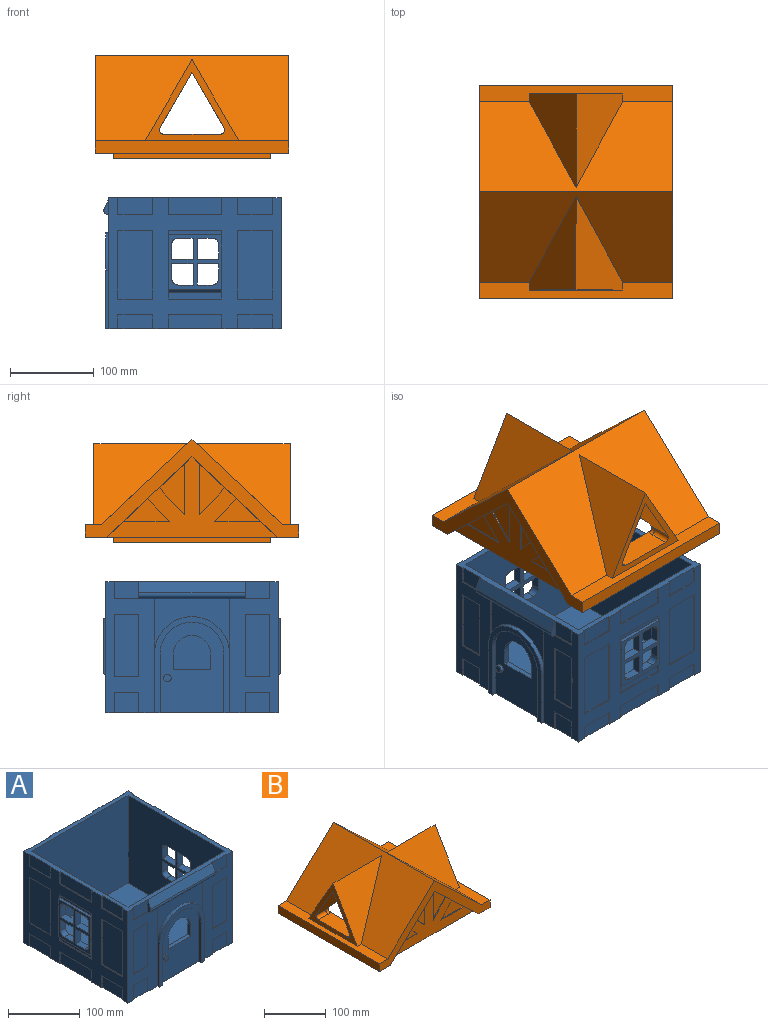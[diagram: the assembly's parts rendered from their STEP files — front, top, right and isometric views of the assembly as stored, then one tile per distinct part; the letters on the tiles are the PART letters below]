
ASSEMBLY  parts=2 mates=1
PART A: 231 faces, bbox 210.8x211.7x156.2 mm
  f0: plane 66.04x20.32mm, normal (0,1,0), area 1341.9mm2, adj f7,f219,f220,f223
  f1: plane 41.66x20.32mm, normal (0,1,0), area 846.4mm2, adj f7,f216,f217,f218
  f2: plane 66.04x20.32mm, normal (0,1,0), area 1341.9mm2, adj f6,f210,f211,f212
  f3: plane 41.66x20.32mm, normal (0,1,0), area 846.4mm2, adj f6,f207,f208,f209
  f4: plane 41.66x20.32mm, normal (0,1,0), area 846.4mm2, adj f6,f213,f214,f215
  f5: plane 41.66x20.32mm, normal (0,1,0), area 846.4mm2, adj f7,f204,f205,f206
  f6: plane 209.55x205.74mm, normal (0,0,-1), area 41647mm2, adj f2,f3,f4,f14,f15,f16,f19,f21
  f7: plane 205.74x205.74mm, normal (0,0,1), area 5328.9mm2, adj f0,f1,f5,f8,f15,f22,f23,f24
  f8: plane 20.32x1.27mm, normal (-1,0,0), area 25.8mm2, adj f7,f9,f15,f41
  f9: plane 28.7x1.27mm, normal (0,0,1), area 36.5mm2, adj f8,f15,f41,f104
  f10: plane 28.7x1.27mm, normal (0,0,-1), area 36.5mm2, adj f11,f15,f17,f18
  f11: plane 74.17x1.27mm, normal (-1,0,0), area 94.2mm2, adj f10,f12,f15,f17
  f12: plane 28.7x1.27mm, normal (0,0,1), area 36.5mm2, adj f11,f15,f17,f18
  f13: plane 28.7x1.27mm, normal (0,0,-1), area 36.5mm2, adj f14,f15,f16,f19
  f14: plane 24.13x1.27mm, normal (-1,0,0), area 30.6mm2, adj f6,f13,f15,f16
  f15: plane 156.21x58.17mm, normal (0,-1,0), area 5299.6mm2, adj f6,f7,f8,f9,f10,f11,f12,f13
  f16: plane 28.7x24.13mm, normal (0,-1,0), area 692.6mm2, adj f6,f13,f14,f19
  f17: plane 74.17x28.7mm, normal (0,-1,0), area 2128.8mm2, adj f10,f11,f12,f18
  f18: plane 74.17x1.27mm, normal (1,0,0), area 94.2mm2, adj f10,f12,f15,f17
  f19: plane 24.13x1.27mm, normal (1,0,0), area 30.6mm2, adj f6,f13,f15,f16
  f20: plane 74.17x28.7mm, normal (0,-1,0), area 2128.8mm2, adj f30,f151,f152,f153
  f21: plane 28.7x24.13mm, normal (0,-1,0), area 692.6mm2, adj f6,f103,f149,f150
  f22: plane 41.66x20.32mm, normal (-1,0,0), area 846.4mm2, adj f7,f176,f177,f178
  f23: plane 63.5x20.32mm, normal (-1,0,0), area 1290.3mm2, adj f7,f173,f174,f175
  f24: plane 41.66x20.32mm, normal (-1,0,0), area 846.4mm2, adj f7,f170,f171,f172
  f25: plane 41.66x20.32mm, normal (-1,0,0), area 846.4mm2, adj f6,f167,f168,f169
  f26: plane 63.5x4.06mm, normal (-1,0,0), area 258.1mm2, adj f145,f146,f182,f230
  f27: plane 63.5x5.33mm, normal (-1,0,0), area 338.7mm2, adj f81,f158,f159,f160
  f28: plane 63.5x20.32mm, normal (-1,0,0), area 1290.3mm2, adj f6,f164,f165,f166
  f29: plane 41.66x20.32mm, normal (-1,0,0), area 846.4mm2, adj f6,f179,f180,f181
  f30: plane 74.17x1.27mm, normal (-1,0,0), area 94.2mm2, adj f20,f108,f151,f153
  f31: plane 20.32x7.27mm, normal (-1,0,0), area 95.6mm2, adj f7,f43,f44,f105,f109,f147
  f32: plane 63.5x20.32mm, normal (1,0,0), area 1290.3mm2, adj f7,f121,f137,f140
  f33: plane 41.66x20.32mm, normal (1,0,0), area 846.4mm2, adj f7,f134,f135,f136
  f34: plane 63.5x16.51mm, normal (1,0,0), area 1048.4mm2, adj f6,f128,f129,f130
  f35: plane 41.66x16.51mm, normal (1,0,0), area 687.7mm2, adj f6,f125,f126,f127
  f36: plane 41.66x20.32mm, normal (1,0,0), area 846.4mm2, adj f7,f122,f123,f124
  f37: plane 41.66x16.51mm, normal (1,0,0), area 687.7mm2, adj f6,f131,f132,f133
  f38: plane 63.5x7.87mm, normal (1,0,0), area 500mm2, adj f110,f111,f141,f229
  f39: plane 63.5x5.33mm, normal (1,0,0), area 338.7mm2, adj f61,f112,f113,f114
  f40: plane 89.41x66.04mm, normal (0,-1,0), area 2765.4mm2, adj f43,f52,f106,f107
  f41: plane 28.7x20.32mm, normal (0,-1,0), area 583.2mm2, adj f7,f8,f9,f104
  f42: plane 69.85x3.81mm, normal (1,0,0), area 266.1mm2, adj f6,f15,f52,f56
  f43: plane 127x2.19mm, normal (0,0,-1), area 229.9mm2, adj f15,f31,f40,f104,f106,f107,f108,f109
  f44: plane 28.7x20.32mm, normal (0,-1,0), area 583.2mm2, adj f7,f31,f147,f148
  f45: plane 190.5x149.86mm, normal (1,0,0), area 26017.5mm2, adj f7,f48,f49,f50,f83,f84,f85,f86
  f46: plane 190.5x149.86mm, normal (-1,0,0), area 26017.5mm2, adj f7,f48,f49,f50,f63,f64,f65,f66
  f47: plane 107.95x76.2mm, normal (0,-1,0), area 5923.2mm2, adj f6,f51,f54,f55,f57,f58,f59,f60
  f48: plane 190.5x149.86mm, normal (0,1,0), area 26935.1mm2, adj f7,f45,f46,f50,f57,f58,f59,f60
  f49: plane 190.5x149.86mm, normal (0,-1,0), area 28548.3mm2, adj f7,f45,f46,f50
  f50: plane 190.5x190.5mm, normal (0,0,1), area 36290.2mm2, adj f45,f46,f48,f49
  f51: plane 69.85x5.08mm, normal (-1,0,0), area 354.8mm2, adj f6,f47,f55,f56
  f52: cylinder r=44.7mm len=89.41mm, axis (0,1,0), area 713.4mm2, adj f40,f42,f53,f56,f106,f107
  f53: plane 69.85x3.81mm, normal (-1,0,0), area 266.1mm2, adj f6,f52,f56,f108
  f54: plane 69.85x5.08mm, normal (1,0,0), area 354.8mm2, adj f6,f47,f55,f56
  f55: cylinder r=38.1mm len=76.2mm, axis (0,1,0), area 608mm2, adj f47,f51,f54,f56
  f56: plane 114.55x89.41mm, normal (0,-1,0), area 1781.6mm2, adj f6,f42,f51,f52,f53,f54,f55
  f57: plane 18.84x6.35mm, normal (1,0,0), area 119.6mm2, adj f47,f48,f58,f59
  f58: cylinder r=22.23mm len=44.45mm, axis (0,-1,0), area 443.4mm2, adj f47,f48,f57,f60
  f59: plane 44.45x6.35mm, normal (0,0,1), area 282.3mm2, adj f47,f48,f57,f60
  f60: plane 18.84x6.35mm, normal (-1,0,0), area 119.6mm2, adj f47,f48,f58,f59
  f61: plane 63.5x3.81mm, normal (0,0,1), area 241.9mm2, adj f39,f62,f79,f80,f112,f114
  f62: plane 67.31x2.54mm, normal (0,-1,0), area 167.7mm2, adj f61,f80,f142,f229
  f63: plane 17.78x10.16mm, normal (0,1,0), area 180.6mm2, adj f46,f75,f80,f194
  f64: plane 17.78x10.16mm, normal (0,0,-1), area 180.6mm2, adj f46,f65,f80,f194
  f65: plane 25.4x10.16mm, normal (0,-1,0), area 258.1mm2, adj f46,f64,f75,f80
  f66: plane 17.78x10.16mm, normal (0,0,1), area 180.6mm2, adj f46,f76,f80,f193
  f67: plane 17.78x10.16mm, normal (0,1,0), area 180.6mm2, adj f46,f68,f80,f193
  f68: plane 25.4x10.16mm, normal (0,0,-1), area 258.1mm2, adj f46,f67,f76,f80
  f69: plane 25.4x10.16mm, normal (0,0,1), area 258.1mm2, adj f46,f70,f77,f80
  f70: plane 25.4x10.16mm, normal (0,1,0), area 258.1mm2, adj f46,f69,f71,f80
  f71: plane 17.78x10.16mm, normal (0,0,-1), area 180.6mm2, adj f46,f70,f80,f192
  f72: plane 17.78x10.16mm, normal (0,0,1), area 180.6mm2, adj f46,f73,f80,f191
  f73: plane 25.4x10.16mm, normal (0,1,0), area 258.1mm2, adj f46,f72,f74,f80
  f74: plane 25.4x10.16mm, normal (0,0,-1), area 258.1mm2, adj f46,f73,f78,f80
  f75: plane 25.4x10.16mm, normal (0,0,1), area 258.1mm2, adj f46,f63,f65,f80
  f76: plane 25.4x10.16mm, normal (0,-1,0), area 258.1mm2, adj f46,f66,f68,f80
  f77: plane 17.78x10.16mm, normal (0,-1,0), area 180.6mm2, adj f46,f69,f80,f192
  f78: plane 17.78x10.16mm, normal (0,-1,0), area 180.6mm2, adj f46,f74,f80,f191
  f79: plane 67.31x2.54mm, normal (0,1,0), area 167.7mm2, adj f61,f80,f142,f229
  f80: plane 64.77x63.5mm, normal (1,0,0), area 1582.1mm2, adj f61,f62,f63,f64,f65,f66,f67,f68
  f81: plane 63.5x3.81mm, normal (0,0,1), area 241.9mm2, adj f27,f82,f99,f100,f158,f160
  f82: plane 67.31x2.54mm, normal (0,1,0), area 167.7mm2, adj f81,f100,f154,f230
  f83: plane 17.78x10.16mm, normal (0,-1,0), area 180.6mm2, adj f45,f95,f100,f190
  f84: plane 17.78x10.16mm, normal (0,0,-1), area 180.6mm2, adj f45,f85,f100,f190
  f85: plane 25.4x10.16mm, normal (0,1,0), area 258.1mm2, adj f45,f84,f95,f100
  f86: plane 17.78x10.16mm, normal (0,0,1), area 180.6mm2, adj f45,f96,f100,f189
  f87: plane 17.78x10.16mm, normal (0,-1,0), area 180.6mm2, adj f45,f88,f100,f189
  f88: plane 25.4x10.16mm, normal (0,0,-1), area 258.1mm2, adj f45,f87,f96,f100
  f89: plane 25.4x10.16mm, normal (0,0,1), area 258.1mm2, adj f45,f90,f97,f100
  f90: plane 25.4x10.16mm, normal (0,-1,0), area 258.1mm2, adj f45,f89,f91,f100
  f91: plane 17.78x10.16mm, normal (0,0,-1), area 180.6mm2, adj f45,f90,f100,f188
  f92: plane 17.78x10.16mm, normal (0,0,1), area 180.6mm2, adj f45,f93,f100,f187
  f93: plane 25.4x10.16mm, normal (0,-1,0), area 258.1mm2, adj f45,f92,f94,f100
  f94: plane 25.4x10.16mm, normal (0,0,-1), area 258.1mm2, adj f45,f93,f98,f100
  f95: plane 25.4x10.16mm, normal (0,0,1), area 258.1mm2, adj f45,f83,f85,f100
  f96: plane 25.4x10.16mm, normal (0,1,0), area 258.1mm2, adj f45,f86,f88,f100
  f97: plane 17.78x10.16mm, normal (0,1,0), area 180.6mm2, adj f45,f89,f100,f188
  f98: plane 17.78x10.16mm, normal (0,1,0), area 180.6mm2, adj f45,f94,f100,f187
  f99: plane 67.31x2.54mm, normal (0,-1,0), area 167.7mm2, adj f81,f100,f154,f230
  f100: plane 64.77x63.5mm, normal (-1,0,0), area 1582.1mm2, adj f81,f82,f83,f84,f85,f86,f87,f88
  f101: cylinder r=4.59mm len=9.19mm, axis (0,1,0), area 110mm2, adj f47,f102
  f102: plane 9.19x9.19mm, normal (0,-1,0), area 66.3mm2, adj f101
  f103: plane 24.13x1.27mm, normal (-1,0,0), area 30.6mm2, adj f6,f21,f108,f150
  f104: plane 20.32x7.27mm, normal (1,0,0), area 95.6mm2, adj f7,f9,f41,f43,f105,f109
  f105: plane 127x13.09mm, normal (0,-0.91,0.42), area 1834.7mm2, adj f7,f31,f104,f109
  f106: plane 66.04x1.27mm, normal (-1,0,0), area 83.9mm2, adj f15,f40,f43,f52
  f107: plane 66.04x1.27mm, normal (1,0,0), area 83.9mm2, adj f40,f43,f52,f108
  f108: plane 156.21x58.17mm, normal (0,-1,0), area 5299.6mm2, adj f6,f7,f30,f43,f53,f103,f107,f147
  f109: cylinder r=5.08mm len=127mm, axis (-1,0,0), area 1294.9mm2, adj f31,f43,f104,f105
  f110: plane 9.14x1.27mm, normal (0,1,0), area 10.8mm2, adj f38,f141,f142,f229
  f111: plane 9.14x1.27mm, normal (0,-1,0), area 10.8mm2, adj f38,f141,f142,f229
  f112: plane 5.33x1.27mm, normal (0,1,0), area 6.8mm2, adj f39,f61,f113,f142
  f113: plane 63.5x1.27mm, normal (0,0,-1), area 80.6mm2, adj f39,f112,f114,f142
  f114: plane 5.33x1.27mm, normal (0,-1,0), area 6.8mm2, adj f39,f61,f113,f142
  f115: plane 81.79x1.27mm, normal (0,-1,0), area 103.9mm2, adj f116,f138,f142,f144
  f116: plane 41.66x1.27mm, normal (0,0,1), area 52.9mm2, adj f115,f117,f142,f144
  f117: plane 81.79x1.27mm, normal (0,1,0), area 103.9mm2, adj f116,f138,f142,f144
  f118: plane 41.66x1.27mm, normal (0,0,1), area 52.9mm2, adj f119,f139,f142,f143
  f119: plane 81.79x1.27mm, normal (0,1,0), area 103.9mm2, adj f118,f120,f142,f143
  f120: plane 41.66x1.27mm, normal (0,0,-1), area 52.9mm2, adj f119,f139,f142,f143
  f121: plane 20.32x1.27mm, normal (0,1,0), area 25.8mm2, adj f7,f32,f140,f142
  f122: plane 20.32x1.27mm, normal (0,-1,0), area 25.8mm2, adj f7,f36,f123,f142
  f123: plane 41.66x1.27mm, normal (0,0,1), area 52.9mm2, adj f36,f122,f124,f142
  f124: plane 20.32x1.27mm, normal (0,1,0), area 25.8mm2, adj f7,f36,f123,f142
  f125: plane 16.51x1.27mm, normal (0,1,0), area 21mm2, adj f6,f35,f126,f142
  f126: plane 41.66x1.27mm, normal (0,0,-1), area 52.9mm2, adj f35,f125,f127,f142
  f127: plane 16.51x1.27mm, normal (0,-1,0), area 21mm2, adj f6,f35,f126,f142
  f128: plane 16.51x1.27mm, normal (0,1,0), area 21mm2, adj f6,f34,f129,f142
  f129: plane 63.5x1.27mm, normal (0,0,-1), area 80.6mm2, adj f34,f128,f130,f142
  f130: plane 16.51x1.27mm, normal (0,-1,0), area 21mm2, adj f6,f34,f129,f142
  f131: plane 16.51x1.27mm, normal (0,1,0), area 21mm2, adj f6,f37,f132,f142
  f132: plane 41.66x1.27mm, normal (0,0,-1), area 52.9mm2, adj f37,f131,f133,f142
  f133: plane 16.51x1.27mm, normal (0,-1,0), area 21mm2, adj f6,f37,f132,f142
  f134: plane 20.32x1.27mm, normal (0,-1,0), area 25.8mm2, adj f7,f33,f135,f142
  f135: plane 41.66x1.27mm, normal (0,0,1), area 52.9mm2, adj f33,f134,f136,f142
  f136: plane 20.32x1.27mm, normal (0,1,0), area 25.8mm2, adj f7,f33,f135,f142
  f137: plane 20.32x1.27mm, normal (0,-1,0), area 25.8mm2, adj f7,f32,f140,f142
  f138: plane 41.66x1.27mm, normal (0,0,-1), area 52.9mm2, adj f115,f117,f142,f144
  f139: plane 81.79x1.27mm, normal (0,-1,0), area 103.9mm2, adj f118,f120,f142,f143
  f140: plane 63.5x1.27mm, normal (0,0,1), area 80.6mm2, adj f32,f121,f137,f142
  f141: plane 63.5x1.27mm, normal (0,0,1), area 80.6mm2, adj f38,f110,f111,f142
  f142: plane 205.74x156.21mm, normal (1,0,0), area 14724.1mm2, adj f6,f7,f15,f62,f79,f110,f111,f112
  f143: plane 81.79x41.66mm, normal (1,0,0), area 3407mm2, adj f118,f119,f120,f139
  f144: plane 81.79x41.66mm, normal (1,0,0), area 3407mm2, adj f115,f116,f117,f138
  f145: plane 5.33x1.27mm, normal (0,-1,0), area 6mm2, adj f26,f154,f182,f230
  f146: plane 5.33x1.27mm, normal (0,1,0), area 6mm2, adj f26,f154,f182,f230
  f147: plane 28.7x1.27mm, normal (0,0,1), area 36.5mm2, adj f31,f44,f108,f148
  f148: plane 20.32x1.27mm, normal (1,0,0), area 25.8mm2, adj f7,f44,f108,f147
  f149: plane 24.13x1.27mm, normal (1,0,0), area 30.6mm2, adj f6,f21,f108,f150
  f150: plane 28.7x1.27mm, normal (0,0,-1), area 36.5mm2, adj f21,f103,f108,f149
  f151: plane 28.7x1.27mm, normal (0,0,1), area 36.5mm2, adj f20,f30,f108,f152
  f152: plane 74.17x1.27mm, normal (1,0,0), area 94.2mm2, adj f20,f108,f151,f153
  f153: plane 28.7x1.27mm, normal (0,0,-1), area 36.5mm2, adj f20,f30,f108,f152
  f154: plane 205.74x156.21mm, normal (-1,0,0), area 14724.1mm2, adj f6,f7,f82,f99,f108,f145,f146,f155
  f155: plane 77.98x1.27mm, normal (0,-1,0), area 99mm2, adj f154,f156,f184,f185
  f156: plane 41.66x1.27mm, normal (0,0,-1), area 52.9mm2, adj f154,f155,f157,f185
  f157: plane 77.98x1.27mm, normal (0,1,0), area 99mm2, adj f154,f156,f184,f185
  f158: plane 5.33x1.27mm, normal (0,-1,0), area 6.8mm2, adj f27,f81,f154,f159
  f159: plane 63.5x1.27mm, normal (0,0,-1), area 80.6mm2, adj f27,f154,f158,f160
  f160: plane 5.33x1.27mm, normal (0,1,0), area 6.8mm2, adj f27,f81,f154,f159
  f161: plane 77.98x1.27mm, normal (0,-1,0), area 99mm2, adj f154,f162,f183,f186
  f162: plane 41.66x1.27mm, normal (0,0,-1), area 52.9mm2, adj f154,f161,f163,f186
  f163: plane 77.98x1.27mm, normal (0,1,0), area 99mm2, adj f154,f162,f183,f186
  f164: plane 20.32x1.27mm, normal (0,-1,0), area 25.8mm2, adj f6,f28,f154,f165
  f165: plane 63.5x1.27mm, normal (0,0,-1), area 80.6mm2, adj f28,f154,f164,f166
  f166: plane 20.32x1.27mm, normal (0,1,0), area 25.8mm2, adj f6,f28,f154,f165
  f167: plane 20.32x1.27mm, normal (0,-1,0), area 25.8mm2, adj f6,f25,f154,f168
  f168: plane 41.66x1.27mm, normal (0,0,-1), area 52.9mm2, adj f25,f154,f167,f169
  f169: plane 20.32x1.27mm, normal (0,1,0), area 25.8mm2, adj f6,f25,f154,f168
  f170: plane 20.32x1.27mm, normal (0,1,0), area 25.8mm2, adj f7,f24,f154,f171
  f171: plane 41.66x1.27mm, normal (0,0,1), area 52.9mm2, adj f24,f154,f170,f172
  f172: plane 20.32x1.27mm, normal (0,-1,0), area 25.8mm2, adj f7,f24,f154,f171
  f173: plane 20.32x1.27mm, normal (0,1,0), area 25.8mm2, adj f7,f23,f154,f174
  f174: plane 63.5x1.27mm, normal (0,0,1), area 80.6mm2, adj f23,f154,f173,f175
  f175: plane 20.32x1.27mm, normal (0,-1,0), area 25.8mm2, adj f7,f23,f154,f174
  f176: plane 20.32x1.27mm, normal (0,1,0), area 25.8mm2, adj f7,f22,f154,f177
  f177: plane 41.66x1.27mm, normal (0,0,1), area 52.9mm2, adj f22,f154,f176,f178
  f178: plane 20.32x1.27mm, normal (0,-1,0), area 25.8mm2, adj f7,f22,f154,f177
  f179: plane 20.32x1.27mm, normal (0,-1,0), area 25.8mm2, adj f6,f29,f154,f180
  f180: plane 41.66x1.27mm, normal (0,0,-1), area 52.9mm2, adj f29,f154,f179,f181
  f181: plane 20.32x1.27mm, normal (0,1,0), area 25.8mm2, adj f6,f29,f154,f180
  f182: plane 63.5x1.27mm, normal (0,0,1), area 80.6mm2, adj f26,f145,f146,f154
  f183: plane 41.66x1.27mm, normal (0,0,1), area 52.9mm2, adj f154,f161,f163,f186
  f184: plane 41.66x1.27mm, normal (0,0,1), area 52.9mm2, adj f154,f155,f157,f185
  f185: plane 77.98x41.66mm, normal (-1,0,0), area 3248.3mm2, adj f155,f156,f157,f184
  f186: plane 77.98x41.66mm, normal (-1,0,0), area 3248.3mm2, adj f161,f162,f163,f183
  f187: cylinder r=7.62mm len=10.16mm, axis (1,0,0), area 121.6mm2, adj f45,f92,f98,f100
  f188: cylinder r=7.62mm len=10.16mm, axis (-1,0,0), area 121.6mm2, adj f45,f91,f97,f100
  f189: cylinder r=7.62mm len=10.16mm, axis (-1,0,0), area 121.6mm2, adj f45,f86,f87,f100
  f190: cylinder r=7.62mm len=10.16mm, axis (1,0,0), area 121.6mm2, adj f45,f83,f84,f100
  f191: cylinder r=7.62mm len=10.16mm, axis (-1,0,0), area 121.6mm2, adj f46,f72,f78,f80
  f192: cylinder r=7.62mm len=10.16mm, axis (1,0,0), area 121.6mm2, adj f46,f71,f77,f80
  f193: cylinder r=7.62mm len=10.16mm, axis (1,0,0), area 121.6mm2, adj f46,f66,f67,f80
  f194: cylinder r=7.62mm len=10.16mm, axis (-1,0,0), area 121.6mm2, adj f46,f63,f64,f80
  f195: plane 41.66x1.27mm, normal (0,0,-1), area 52.9mm2, adj f196,f224,f225,f228
  f196: plane 77.98x1.27mm, normal (1,0,0), area 99mm2, adj f195,f197,f225,f228
  f197: plane 41.66x1.27mm, normal (0,0,1), area 52.9mm2, adj f196,f224,f225,f228
  f198: plane 77.98x1.27mm, normal (-1,0,0), area 99mm2, adj f199,f221,f225,f227
  f199: plane 66.04x1.27mm, normal (0,0,-1), area 83.9mm2, adj f198,f200,f225,f227
  f200: plane 77.98x1.27mm, normal (1,0,0), area 99mm2, adj f199,f221,f225,f227
  f201: plane 77.98x1.27mm, normal (-1,0,0), area 99mm2, adj f202,f222,f225,f226
  f202: plane 41.66x1.27mm, normal (0,0,-1), area 52.9mm2, adj f201,f203,f225,f226
  f203: plane 77.98x1.27mm, normal (1,0,0), area 99mm2, adj f202,f222,f225,f226
  f204: plane 20.32x1.27mm, normal (1,0,0), area 25.8mm2, adj f5,f7,f205,f225
  f205: plane 41.66x1.27mm, normal (0,0,1), area 52.9mm2, adj f5,f204,f206,f225
  f206: plane 20.32x1.27mm, normal (-1,0,0), area 25.8mm2, adj f5,f7,f205,f225
  f207: plane 20.32x1.27mm, normal (-1,0,0), area 25.8mm2, adj f3,f6,f208,f225
  f208: plane 41.66x1.27mm, normal (0,0,-1), area 52.9mm2, adj f3,f207,f209,f225
  f209: plane 20.32x1.27mm, normal (1,0,0), area 25.8mm2, adj f3,f6,f208,f225
  f210: plane 20.32x1.27mm, normal (-1,0,0), area 25.8mm2, adj f2,f6,f211,f225
  f211: plane 66.04x1.27mm, normal (0,0,-1), area 83.9mm2, adj f2,f210,f212,f225
  f212: plane 20.32x1.27mm, normal (1,0,0), area 25.8mm2, adj f2,f6,f211,f225
  f213: plane 20.32x1.27mm, normal (-1,0,0), area 25.8mm2, adj f4,f6,f214,f225
  f214: plane 41.66x1.27mm, normal (0,0,-1), area 52.9mm2, adj f4,f213,f215,f225
  f215: plane 20.32x1.27mm, normal (1,0,0), area 25.8mm2, adj f4,f6,f214,f225
  f216: plane 20.32x1.27mm, normal (1,0,0), area 25.8mm2, adj f1,f7,f217,f225
  f217: plane 41.66x1.27mm, normal (0,0,1), area 52.9mm2, adj f1,f216,f218,f225
  f218: plane 20.32x1.27mm, normal (-1,0,0), area 25.8mm2, adj f1,f7,f217,f225
  f219: plane 20.32x1.27mm, normal (1,0,0), area 25.8mm2, adj f0,f7,f220,f225
  f220: plane 66.04x1.27mm, normal (0,0,1), area 83.9mm2, adj f0,f219,f223,f225
  f221: plane 66.04x1.27mm, normal (0,0,1), area 83.9mm2, adj f198,f200,f225,f227
  f222: plane 41.66x1.27mm, normal (0,0,1), area 52.9mm2, adj f201,f203,f225,f226
  f223: plane 20.32x1.27mm, normal (-1,0,0), area 25.8mm2, adj f0,f7,f220,f225
  f224: plane 77.98x1.27mm, normal (-1,0,0), area 99mm2, adj f195,f197,f225,f228
  f225: plane 205.74x156.21mm, normal (0,1,0), area 14422.8mm2, adj f6,f7,f142,f154,f195,f196,f197,f198
  f226: plane 77.98x41.66mm, normal (0,1,0), area 3248.3mm2, adj f201,f202,f203,f222
  f227: plane 77.98x66.04mm, normal (0,1,0), area 5149.7mm2, adj f198,f199,f200,f221
  f228: plane 77.98x41.66mm, normal (0,1,0), area 3248.3mm2, adj f195,f196,f197,f224
  f229: plane 63.5x3.81mm, normal (0.71,0,-0.71), area 342.1mm2, adj f38,f62,f79,f80,f110,f111
  f230: plane 63.5x3.81mm, normal (-0.71,0,-0.71), area 342.1mm2, adj f26,f82,f99,f100,f145,f146
PART B: 92 faces, bbox 254x231.1x123.2 mm
  f0: bspline ~16.69x7.15mm, area 36.6mm2, adj f67,f74,f91
  f1: bspline ~16.69x7.15mm, area 37.1mm2, adj f67,f79,f87
  f2: bspline ~16.69x7.15mm, area 37.1mm2, adj f73,f76,f84
  f3: bspline ~16.69x7.15mm, area 36.6mm2, adj f73,f77,f82
  f4: plane 69.41x29.52mm, normal (0,0,1), area 1995.8mm2, adj f49,f67,f86,f88,f89,f90
  f5: plane 231.14x107.66mm, normal (0.69,0,0.73), area 26378.6mm2, adj f6,f11,f15,f16,f53,f54
  f6: plane 231.14x107.66mm, normal (-0.69,0,0.73), area 26378.6mm2, adj f5,f7,f11,f16,f50,f51
  f7: plane 231.14x19.34mm, normal (0,0,1), area 3447.7mm2, adj f6,f11,f16,f17,f49,f50,f51
  f8: plane 254x231.14mm, normal (0,0,-1), area 18392mm2, adj f9,f10,f11,f12,f13,f14,f16,f17
  f9: plane 101.6x95.88mm, normal (0.69,0,-0.73), area 1876.5mm2, adj f8,f10,f16,f21,f22,f30,f31,f32
  f10: plane 101.6x95.88mm, normal (-0.69,0,-0.73), area 1876.5mm2, adj f8,f9,f16,f23,f24,f26,f27,f28
  f11: plane 254x116.84mm, normal (0,1,0), area 5066.9mm2, adj f5,f6,f7,f8,f12,f13,f14,f15
  f12: plane 101.6x95.88mm, normal (0.69,0,-0.73), area 1876.5mm2, adj f8,f11,f13,f19,f25,f37,f38,f39
  f13: plane 101.6x95.88mm, normal (-0.69,0,-0.73), area 1876.5mm2, adj f8,f11,f12,f18,f20,f35,f36,f41
  f14: plane 231.14x15.24mm, normal (1,0,0), area 3522.6mm2, adj f8,f11,f15,f16
  f15: plane 231.14x19.34mm, normal (0,0,1), area 3447.7mm2, adj f5,f11,f14,f16,f52,f53,f54
  f16: plane 254x116.84mm, normal (0,-1,0), area 5066.9mm2, adj f5,f6,f7,f8,f9,f10,f14,f15
  f17: plane 231.14x15.24mm, normal (-1,0,0), area 3522.6mm2, adj f7,f8,f11,f16
  f18: plane 59.63x29.76mm, normal (0,1,0), area 887.4mm2, adj f13,f41,f42
  f19: plane 59.63x29.76mm, normal (0,1,0), area 887.4mm2, adj f12,f39,f40
  f20: plane 54.55x27.23mm, normal (0,1,0), area 742.6mm2, adj f13,f35,f36
  f21: plane 54.55x27.23mm, normal (0,-1,0), area 742.6mm2, adj f9,f32,f33
  f22: plane 59.63x29.76mm, normal (0,-1,0), area 887.4mm2, adj f9,f30,f31
  f23: plane 59.63x29.76mm, normal (0,-1,0), area 887.4mm2, adj f10,f28,f29
  f24: plane 54.55x27.23mm, normal (0,-1,0), area 742.6mm2, adj f10,f26,f27
  f25: plane 54.55x27.23mm, normal (0,1,0), area 742.6mm2, adj f12,f37,f38
  f26: plane 54.55x1.27mm, normal (0,0,1), area 69.3mm2, adj f10,f24,f27,f34
  f27: plane 27.23x25.7mm, normal (0.73,0,-0.69), area 47.5mm2, adj f10,f24,f26,f34
  f28: plane 31.54x29.76mm, normal (-0.73,0,0.69), area 55.1mm2, adj f10,f23,f29,f34
  f29: plane 59.63x1.27mm, normal (1,0,0), area 75.7mm2, adj f10,f23,f28,f34
  f30: plane 59.63x1.27mm, normal (-1,0,0), area 75.7mm2, adj f9,f22,f31,f34
  f31: plane 31.54x29.76mm, normal (0.73,0,0.69), area 55.1mm2, adj f9,f22,f30,f34
  f32: plane 27.23x25.7mm, normal (-0.73,0,-0.69), area 47.5mm2, adj f9,f21,f33,f34
  f33: plane 54.55x1.27mm, normal (0,0,1), area 69.3mm2, adj f9,f21,f32,f34
  f34: plane 203.2x95.88mm, normal (0,-1,0), area 6481.7mm2, adj f8,f9,f10,f26,f27,f28,f29,f30
  f35: plane 27.23x25.7mm, normal (0.73,0,-0.69), area 47.5mm2, adj f13,f20,f36,f43
  f36: plane 54.55x1.27mm, normal (0,0,1), area 69.3mm2, adj f13,f20,f35,f43
  f37: plane 54.55x1.27mm, normal (0,0,1), area 69.3mm2, adj f12,f25,f38,f43
  f38: plane 27.23x25.7mm, normal (-0.73,0,-0.69), area 47.5mm2, adj f12,f25,f37,f43
  f39: plane 31.54x29.76mm, normal (0.73,0,0.69), area 55.1mm2, adj f12,f19,f40,f43
  f40: plane 59.63x1.27mm, normal (-1,0,0), area 75.7mm2, adj f12,f19,f39,f43
  f41: plane 59.63x1.27mm, normal (1,0,0), area 75.7mm2, adj f13,f18,f42,f43
  f42: plane 31.54x29.76mm, normal (-0.73,0,0.69), area 55.1mm2, adj f13,f18,f41,f43
  f43: plane 203.2x95.88mm, normal (0,1,0), area 6481.7mm2, adj f8,f12,f13,f35,f36,f37,f38,f39
  f44: plane 187.5x6.35mm, normal (0,-1,0), area 1190.6mm2, adj f8,f45,f47,f48
  f45: plane 187.5x6.35mm, normal (-1,0,0), area 1190.6mm2, adj f8,f44,f46,f48
  f46: plane 187.5x6.35mm, normal (0,1,0), area 1190.6mm2, adj f8,f45,f47,f48
  f47: plane 187.5x6.35mm, normal (1,0,0), area 1190.6mm2, adj f8,f44,f46,f48
  f48: plane 187.5x187.5mm, normal (0,0,-1), area 4689.8mm2, adj f44,f45,f46,f47,f58,f59,f62,f63
  f49: plane 111.45x96.52mm, normal (-1,0,0), area 2281.4mm2, adj f4,f7,f50,f51,f55,f57,f86,f89
  f50: plane 111.46x96.52mm, normal (0,0.87,0.5), area 6722.7mm2, adj f6,f7,f49,f51
  f51: plane 111.46x96.52mm, normal (0,-0.87,0.5), area 6722.7mm2, adj f6,f7,f49,f50
  f52: plane 111.45x96.52mm, normal (1,0,0), area 2281.4mm2, adj f15,f53,f54,f55,f56,f57,f80,f83
  f53: plane 111.46x96.52mm, normal (0,-0.87,0.5), area 6722.7mm2, adj f5,f15,f52,f54
  f54: plane 111.46x96.52mm, normal (0,0.87,0.5), area 6722.7mm2, adj f5,f15,f52,f53
  f55: plane 233.68x66.04mm, normal (0,0.87,-0.5), area 16252.1mm2, adj f49,f52,f57,f77,f78,f79,f80,f86
  f56: plane 69.41x29.52mm, normal (0,0,1), area 1995.8mm2, adj f52,f73,f80,f81,f83,f85
  f57: plane 233.68x66.04mm, normal (0,-0.87,-0.5), area 16252.1mm2, adj f49,f52,f55,f74,f75,f76,f83,f89
  f58: plane 154.48x27.94mm, normal (1,0,0), area 4316.2mm2, adj f48,f64,f66,f67
  f59: plane 154.48x27.94mm, normal (-1,0,0), area 4316.2mm2, adj f48,f69,f70,f73
  f60: plane 154.48x32.51mm, normal (0,0,-1), area 5022.7mm2, adj f67,f68,f73,f78
  f61: plane 154.48x32.51mm, normal (0,0,-1), area 5022.7mm2, adj f67,f71,f73,f75
  f62: plane 154.48x27.94mm, normal (0,1,0), area 4316.2mm2, adj f48,f64,f68,f69
  f63: plane 154.48x27.94mm, normal (0,-1,0), area 4316.2mm2, adj f48,f66,f70,f71
  f64: cylinder r=10.16mm len=27.94mm, axis (0,0,1), area 445.9mm2, adj f48,f58,f62,f65
  f65: sphere r=10.16mm, area 103.2mm2, adj f64,f67,f68
  f66: cylinder r=10.16mm len=35.12mm, axis (0,0,1), area 503.2mm2, adj f48,f58,f63,f67,f71
  f67: cylinder r=10.16mm len=161.66mm, axis (0,1,0), area 1039.4mm2, adj f0,f1,f4,f58,f60,f61,f65,f66
  f68: cylinder r=10.16mm len=154.48mm, axis (-1,0,0), area 2465.4mm2, adj f60,f62,f65,f72
  f69: cylinder r=10.16mm len=27.94mm, axis (0,0,1), area 445.9mm2, adj f48,f59,f62,f72
  f70: cylinder r=10.16mm len=35.12mm, axis (0,0,1), area 503.2mm2, adj f48,f59,f63,f71,f73
  f71: cylinder r=10.16mm len=168.85mm, axis (1,0,0), area 2580mm2, adj f61,f63,f66,f67,f70,f73
  f72: sphere r=10.16mm, area 162.1mm2, adj f68,f69,f73
  f73: cylinder r=10.16mm len=161.66mm, axis (0,-1,0), area 1039.4mm2, adj f2,f3,f56,f59,f60,f61,f70,f71
  f74: bspline ~26.83x24.77mm, area 179.8mm2, adj f0,f57,f67,f75,f90,f91
  f75: cylinder r=12.7mm len=154.48mm, axis (1,0,0), area 2054.5mm2, adj f57,f61,f74,f76
  f76: bspline ~24.77x23.86mm, area 180.4mm2, adj f2,f57,f73,f75,f84,f85
  f77: bspline ~24.77x23.86mm, area 179.8mm2, adj f3,f55,f73,f78,f81,f82
  f78: cylinder r=12.7mm len=154.48mm, axis (-1,0,0), area 2054.5mm2, adj f55,f60,f77,f79
  f79: bspline ~24.77x23.86mm, area 180.4mm2, adj f1,f55,f67,f78,f87,f88
  f80: cylinder r=5.08mm len=22.56mm, axis (-1,0,0), area 240mm2, adj f52,f55,f56,f81
  f81: bspline ~13.75x11.93mm, area 67.6mm2, adj f56,f77,f80,f82
  f82: bspline ~8.59x8.03mm, area 35mm2, adj f3,f73,f77,f81
  f83: cylinder r=5.08mm len=22.56mm, axis (-1,0,0), area 240mm2, adj f52,f56,f57,f85
  f84: bspline ~8.59x8mm, area 35mm2, adj f2,f73,f76,f85
  f85: bspline ~13.75x11.93mm, area 67.6mm2, adj f56,f76,f83,f84
  f86: cylinder r=5.08mm len=22.56mm, axis (-1,0,0), area 240mm2, adj f4,f49,f55,f88
  f87: bspline ~8.59x8mm, area 35mm2, adj f1,f67,f79,f88
  f88: bspline ~13.75x9.66mm, area 67.6mm2, adj f4,f79,f86,f87
  f89: cylinder r=5.08mm len=22.56mm, axis (-1,0,0), area 240mm2, adj f4,f49,f57,f90
  f90: bspline ~13.75x9.66mm, area 67.6mm2, adj f4,f74,f89,f91
  f91: bspline ~8.59x8.02mm, area 35mm2, adj f0,f67,f74,f90
PLACE A rot(axis=(0,0,-1),90deg) t=(-77.41,74.06,-34.99)mm
PLACE B rot(axis=(0,0,-1),90deg) t=(-81.24,74.06,17.82)mm
MATE slider B.f61 <-> A.f50  axis (0,0,-1) through (3.18,62.23,205.78)mm
